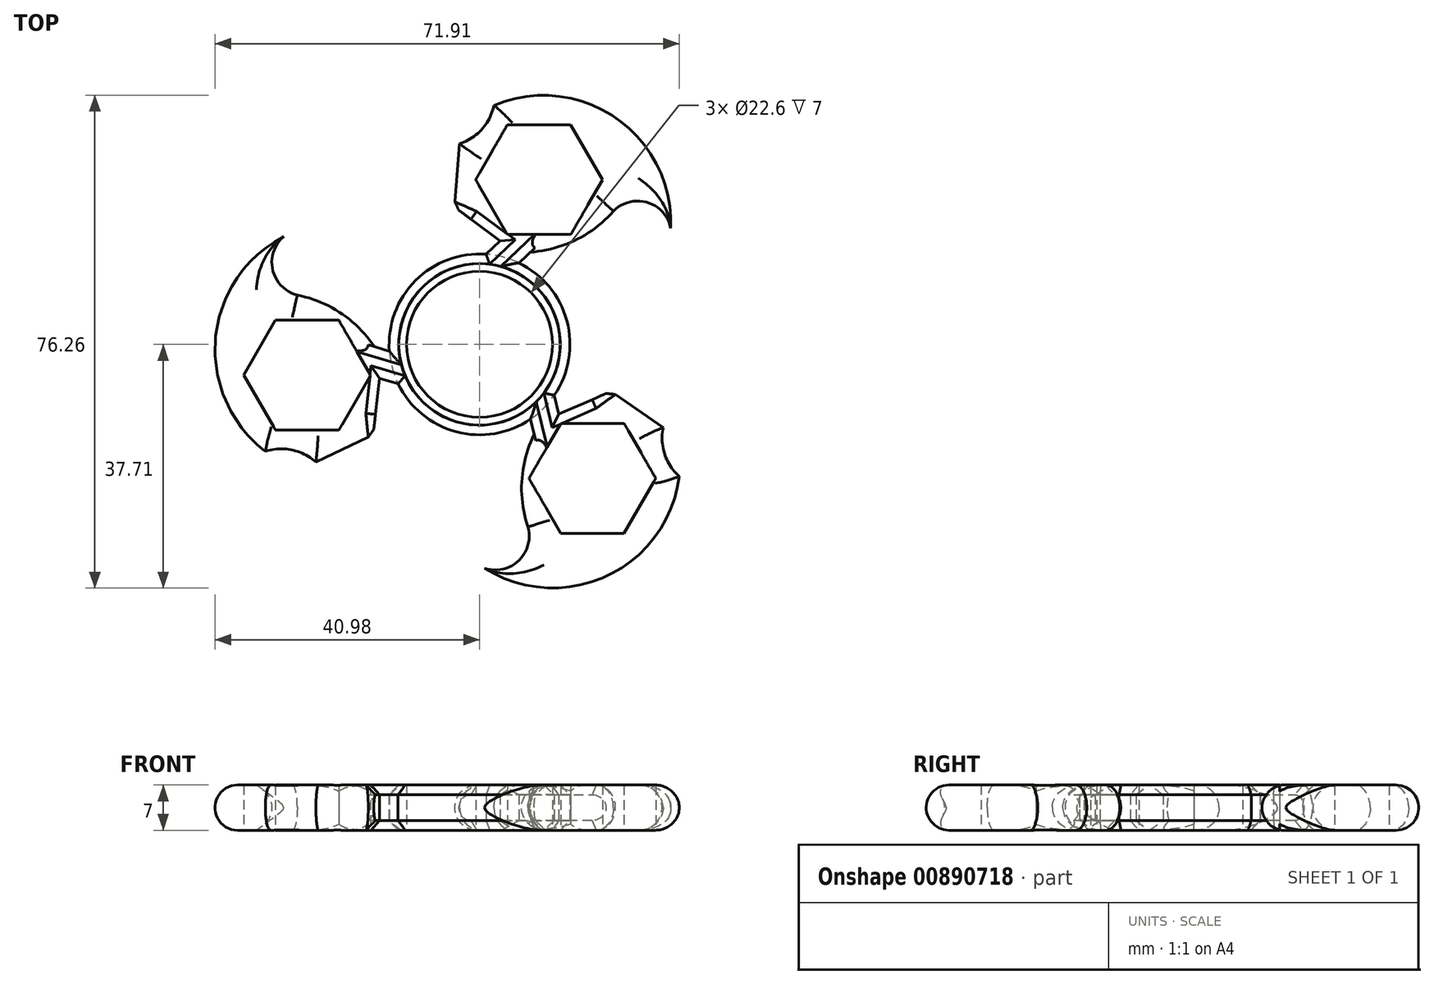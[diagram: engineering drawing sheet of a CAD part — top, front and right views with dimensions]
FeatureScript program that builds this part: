
annotation { "Feature Type Name" : "Feature", "Feature Type Description" : "" }
export const myFeature = defineFeature(function(context is Context, id is Id, definition is map)
    precondition{}
    {
        {
            var Q0;
            Q0=qCreatedBy(makeId("Top.planeOp"),FACE);
            var sketch = newSketch(context, id + "F0", { "sketchPlane" : qUnion([Q0])});
            skCircle(sketch, "E0", {"center": v(0, 0) * mm, "radius": 11.3 * mm});
            skCircle(sketch, "E1.cCircle", {"center": v(9.22, 25.5) * mm, "radius": 8.5 * mm, "construction": true});
            skPoint(sketch, "E1.cCircle.centerSnap0", {"position": v(9.22, 35.06) * mm});
            skLineSegment(sketch, "E1.0", {"start": v(4.31, 34) * mm, "end": v(14.13, 34) * mm});
            skLineSegment(sketch, "E1.1", {"start": v(14.13, 34) * mm, "end": v(19.04, 25.5) * mm});
            skLineSegment(sketch, "E1.2", {"start": v(19.04, 25.5) * mm, "end": v(14.13, 17) * mm});
            skLineSegment(sketch, "E1.3", {"start": v(14.13, 17) * mm, "end": v(4.31, 17) * mm});
            skLineSegment(sketch, "E1.4", {"start": v(4.31, 17) * mm, "end": v(-0.6, 25.5) * mm});
            skLineSegment(sketch, "E1.5", {"start": v(-0.6, 25.5) * mm, "end": v(4.31, 34) * mm});
            skPoint(sketch, "E1.0.midPoint", {"position": v(9.22, 34) * mm});
            skPoint(sketch, "E2.endSnap0", {"position": v(9.22, 17) * mm});
            skPoint(sketch, "E3", {"position": v(2.56, 15.49) * mm});
            skPoint(sketch, "E4", {"position": v(9.93, 17.02) * mm});
            skPoint(sketch, "E5.startSnap0", {"position": v(16.58, 29.75) * mm});
            skPoint(sketch, "E6.endSnap0", {"position": v(16.58, 21.25) * mm});
            skArc(sketch, "E7", {"start": v(29.6, 17.98) * mm, "mid": v(21.15, 35.02) * mm, "end": v(2.23, 37) * mm});
            skLineSegment(sketch, "E8", {"start": v(-3.9, 21.26) * mm, "end": v(-3.08, 31.05) * mm});
            skArc(sketch, "E9", {"start": v(-3.08, 31.05) * mm, "mid": v(0.37, 33.32) * mm, "end": v(2.23, 37) * mm});
            skCircle(sketch, "E10", {"center": v(0, 0) * mm, "radius": 14 * mm});
            skLineSegment(sketch, "E11", {"start": v(1.02, 13.96) * mm, "end": v(3.21, 16.05) * mm});
            skLineSegment(sketch, "E12", {"start": v(3.21, 16.05) * mm, "end": v(-3.9, 21.26) * mm});
            skLineSegment(sketch, "E13", {"start": v(6.07, 12.61) * mm, "end": v(7.81, 14.27) * mm});
            skArc(sketch, "E14", {"start": v(7.81, 14.27) * mm, "mid": v(14.9, 16.17) * mm, "end": v(20.73, 20.62) * mm});
            skArc(sketch, "E15", {"start": v(29.6, 17.98) * mm, "mid": v(25.97, 21.99) * mm, "end": v(20.73, 20.62) * mm});
            skSolve(sketch);
        }
        {
            var Q0;
            Q0=makeQuery(id+"F0.imprint","IMPRINT",FACE,{"disambiguationData":[TD([[makeQuery(id+"F0.imprint","IMPRINT",EDGE,{"derivedFrom":sQuery(id+"F0.wireOp",EDGE,"E1.0")}),1.0]])]});
            var Q1;
            Q1=makeQuery(id+"F0.imprint","IMPRINT",FACE,{"disambiguationData":[TD([[makeQuery(id+"F0.imprint","IMPRINT",EDGE,{"derivedFrom":sQuery(id+"F0.wireOp",EDGE,"E0")}),-1.0]])]});
            extrude(context, id + "F1", {"entities" : qUnion([Q0, Q1]), "depth" : 7 * mm, "offsetDistance" : 25 * mm});
        }
        {
            var Q0;
            Q0=makeQuery(id+"F1.opExtrude","CAP_EDGE",EDGE,{"disambiguationData":[OSD([sQuery(id+"F0.wireOp",EDGE,"E7")])],"isStart":false});
            var Q1;
            Q1=makeQuery(id+"F1.opExtrude","CAP_EDGE",EDGE,{"disambiguationData":[OSD([sQuery(id+"F0.wireOp",EDGE,"E7")])],"isStart":true});
            var Q2;
            Q2=makeQuery(id+"F1.opExtrude","CAP_EDGE",EDGE,{"disambiguationData":[OSD([sQuery(id+"F0.wireOp",EDGE,"E9")])],"isStart":false});
            var Q3;
            Q3=makeQuery(id+"F1.opExtrude","CAP_EDGE",EDGE,{"disambiguationData":[OSD([sQuery(id+"F0.wireOp",EDGE,"E9")])],"isStart":true});
            var Q4;
            Q4=makeQuery(id+"F1.opExtrude","CAP_EDGE",EDGE,{"disambiguationData":[OSD([sQuery(id+"F0.wireOp",EDGE,"E8")])],"isStart":true});
            var Q5;
            Q5=makeQuery(id+"F1.opExtrude","CAP_EDGE",EDGE,{"disambiguationData":[OSD([sQuery(id+"F0.wireOp",EDGE,"E8")])],"isStart":false});
            var Q6;
            Q6=makeQuery(id+"F1.opExtrude","CAP_EDGE",EDGE,{"disambiguationData":[OSD([sQuery(id+"F0.wireOp",EDGE,"E15")])],"isStart":false});
            var Q7;
            Q7=makeQuery(id+"F1.opExtrude","CAP_EDGE",EDGE,{"disambiguationData":[OSD([sQuery(id+"F0.wireOp",EDGE,"E15")])],"isStart":true});
            var Q8;
            Q8=makeQuery(id+"F1.opExtrude","CAP_EDGE",EDGE,{"disambiguationData":[OSD([sQuery(id+"F0.wireOp",EDGE,"E14")])],"isStart":false});
            var Q9;
            Q9=makeQuery(id+"F1.opExtrude","CAP_EDGE",EDGE,{"disambiguationData":[OSD([sQuery(id+"F0.wireOp",EDGE,"E14")])],"isStart":true});
            fillet(context, id + "F2", {"entities" : qUnion([Q0, Q1, Q2, Q3, Q4, Q5, Q6, Q7, Q8, Q9]), "radius" : 3.5 * mm, "tangentPropagation" : true, "allowEdgeOverflow" : false});
        }
        {
            var Q0;
            Q0=makeQuery(id+"F1.opExtrude","CAP_EDGE",EDGE,{"disambiguationData":[OSD([sQuery(id+"F0.wireOp",EDGE,"E13")])],"isStart":false});
            var Q1;
            Q1=makeQuery(id+"F1.opExtrude","CAP_EDGE",EDGE,{"disambiguationData":[OSD([sQuery(id+"F0.wireOp",EDGE,"E13")])],"isStart":true});
            var Q2;
            Q2=makeQuery(id+"F1.opExtrude","CAP_EDGE",EDGE,{"disambiguationData":[OSD([sQuery(id+"F0.wireOp",EDGE,"E11")])],"isStart":true});
            var Q3;
            Q3=makeQuery(id+"F1.opExtrude","CAP_EDGE",EDGE,{"disambiguationData":[OSD([sQuery(id+"F0.wireOp",EDGE,"E11")])],"isStart":false});
            var Q4;
            Q4=makeQuery(id+"F1.opExtrude","CAP_EDGE",EDGE,{"disambiguationData":[OSD([sQuery(id+"F0.wireOp",EDGE,"E10")])],"isStart":false});
            var Q5;
            Q5=makeQuery(id+"F1.opExtrude","CAP_EDGE",EDGE,{"disambiguationData":[OSD([sQuery(id+"F0.wireOp",EDGE,"E10")])],"isStart":true});
            var Q6;
            Q6=makeQuery(id+"F1.opExtrude","CAP_EDGE",EDGE,{"disambiguationData":[OSD([sQuery(id+"F0.wireOp",EDGE,"E12")])],"isStart":false});
            chamfer(context, id + "F3", {"entities" : qUnion([Q0, Q1, Q2, Q3, Q4, Q5, Q6]), "width" : 1.5 * mm, "tangentPropagation" : true});
        }
        {
            var Q0;
            Q0=makeQuery(id+"F1.opExtrude","SWEPT_BODY",BODY,{"disambiguationData":[OSD([sQuery(id+"F0.wireOp",EDGE,"E0"),sQuery(id+"F0.wireOp",EDGE,"E1.0"),sQuery(id+"F0.wireOp",EDGE,"E1.1"),sQuery(id+"F0.wireOp",EDGE,"E1.2"),sQuery(id+"F0.wireOp",EDGE,"E1.3"),sQuery(id+"F0.wireOp",EDGE,"E1.4"),sQuery(id+"F0.wireOp",EDGE,"E1.5"),sQuery(id+"F0.wireOp",EDGE,"E7"),sQuery(id+"F0.wireOp",EDGE,"E8"),sQuery(id+"F0.wireOp",EDGE,"E9"),sQuery(id+"F0.wireOp",EDGE,"E10"),sQuery(id+"F0.wireOp",EDGE,"E11"),sQuery(id+"F0.wireOp",EDGE,"E12"),sQuery(id+"F0.wireOp",EDGE,"E13"),sQuery(id+"F0.wireOp",EDGE,"E14"),sQuery(id+"F0.wireOp",EDGE,"E15")])]});
            var Q1;
            Q1=makeQuery(id+"F1.opExtrude","CAP_EDGE",EDGE,{"disambiguationData":[OSD([sQuery(id+"F0.wireOp",EDGE,"E0")])],"isStart":false});
            circularPattern(context, id + "F4", {"entities" : qUnion([Q0]), "axis" : qUnion([Q1]), "angle" : 360 * degree, "instanceCount" : 3, "equalSpace" : true});
        }
    });
